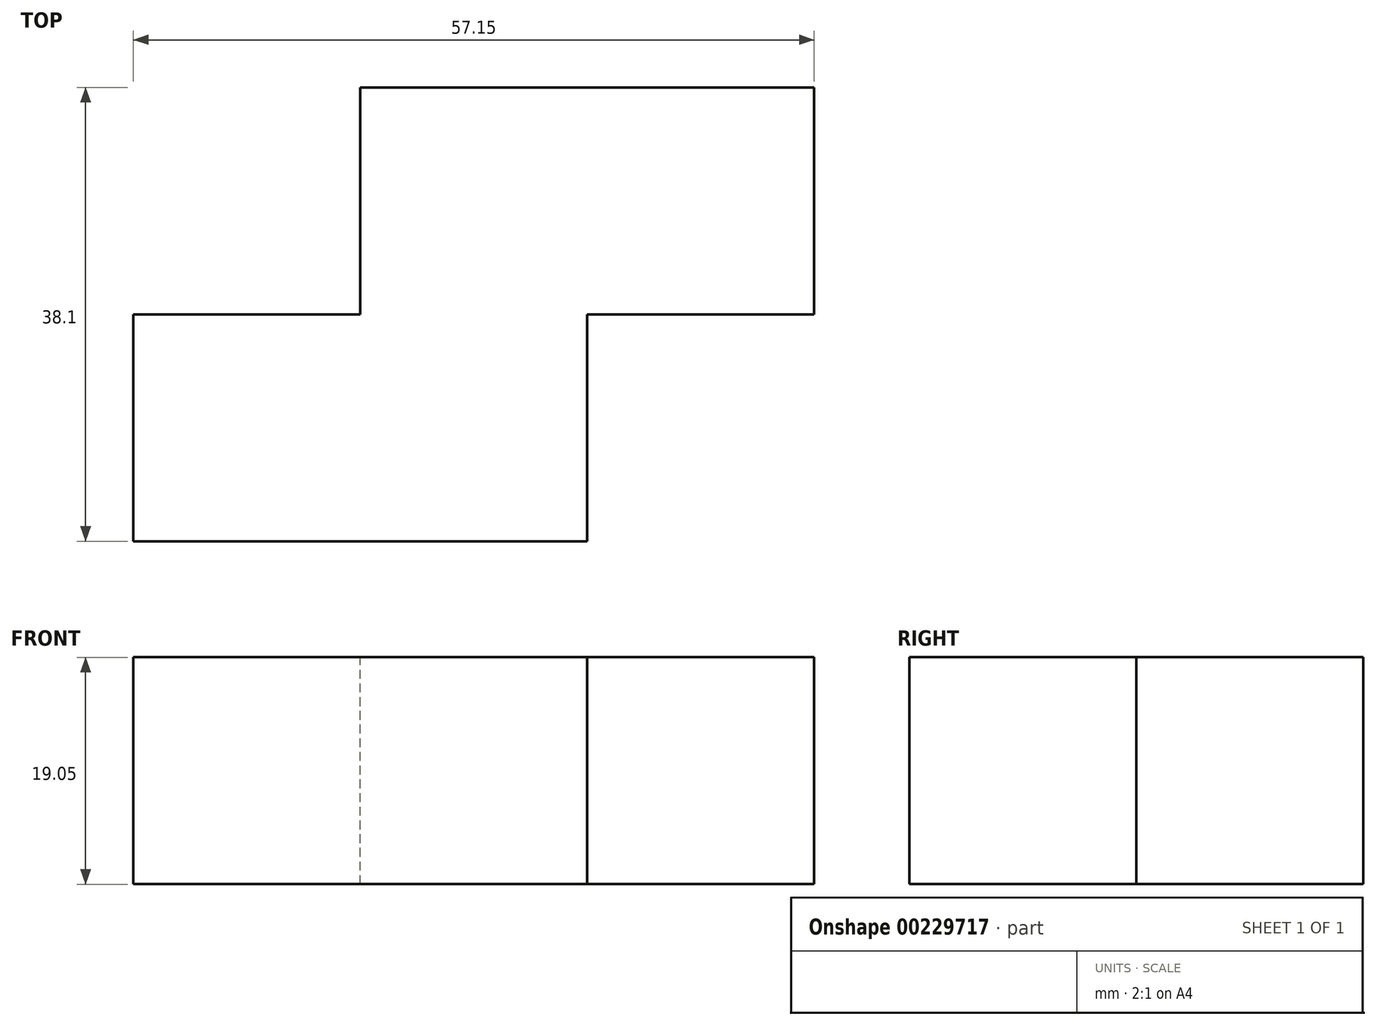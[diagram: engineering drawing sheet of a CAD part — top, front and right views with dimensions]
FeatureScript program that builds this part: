
annotation { "Feature Type Name" : "Feature", "Feature Type Description" : "" }
export const myFeature = defineFeature(function(context is Context, id is Id, definition is map)
    precondition{}
    {
        {
            var Q0;
            Q0=qCreatedBy(makeId("Front.planeOp"),FACE);
            var sketch = newSketch(context, id + "F0", { "sketchPlane" : qUnion([Q0])});
            skLineSegment(sketch, "E0.bottom", {"start": v(-17.07, 9.14) * mm, "end": v(21.03, 9.14) * mm});
            skLineSegment(sketch, "E0.top", {"start": v(-17.07, -9.9) * mm, "end": v(21.03, -9.9) * mm});
            skLineSegment(sketch, "E0.left", {"start": v(-17.07, 9.14) * mm, "end": v(-17.07, -9.9) * mm});
            skLineSegment(sketch, "E0.right", {"start": v(21.03, 9.14) * mm, "end": v(21.03, -9.9) * mm});
            skSolve(sketch);
        }
        {
            var Q0;
            Q0=makeQuery(id+"F0.imprint","IMPRINT",FACE,{"disambiguationData":[TD([[makeQuery(id+"F0.imprint","IMPRINT",EDGE,{"derivedFrom":sQuery(id+"F0.wireOp",EDGE,"E0.bottom")}),-1.0]])]});
            extrude(context, id + "F1", {"entities" : qUnion([Q0]), "depth" : 19.05 * mm});
        }
        {
            var Q0;
            Q0=makeQuery(id+"F1.opExtrude","SWEPT_FACE",FACE,{"disambiguationData":[OSD([sQuery(id+"F0.wireOp",EDGE,"E0.bottom")])]});
            var sketch = newSketch(context, id + "F2", { "sketchPlane" : qUnion([Q0])});
            skLineSegment(sketch, "E1.bottom", {"start": v(1.98, 0) * mm, "end": v(40.08, 0) * mm});
            skLineSegment(sketch, "E1.top", {"start": v(1.98, 19.05) * mm, "end": v(40.08, 19.05) * mm});
            skLineSegment(sketch, "E1.left", {"start": v(1.98, 0) * mm, "end": v(1.98, 19.05) * mm});
            skLineSegment(sketch, "E1.right", {"start": v(40.08, 0) * mm, "end": v(40.08, 19.05) * mm});
            skSolve(sketch);
        }
        {
            var Q0;
            Q0=makeQuery(id+"F2.imprint","IMPRINT",FACE,{"disambiguationData":[TD([[makeQuery(id+"F2.imprint","IMPRINT",EDGE,{"derivedFrom":sQuery(id+"F2.wireOp",EDGE,"E1.top")}),-1.0]])]});
            extrude(context, id + "F3", {"entities" : qUnion([Q0]), "operationType" : NewBodyOperationType.ADD, "oppositeDirection" : true, "depth" : 19.05 * mm});
        }
    });
